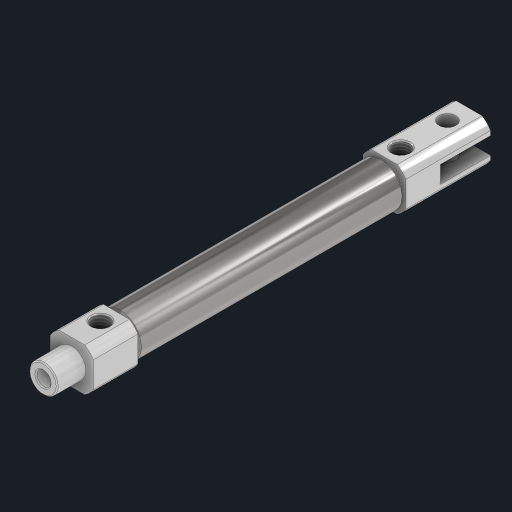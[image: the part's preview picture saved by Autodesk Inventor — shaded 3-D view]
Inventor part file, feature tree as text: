
AUTODESK INVENTOR PART (.ipt)
format: ipt  version: 2023 (Build 270158030, 158C)  size: 207,872 bytes
history: mixed  units: in
note: dims shown in document units (in); Inventor stores cm internally (conversion verified against a paired STEP export)
features: thread x2, extrude x1, sketch x1, other x1, imported_body x1
ambient origin geometry x8: Origin, YZ Plane, XZ Plane, XY Plane, X Axis, Y Axis, Z Axis, Center Point
bodies: Solid1 (imported_parasolid)
feature tree (6):
  thread  "Thread1"  [1 undecoded]
  thread  "Thread2"  [1 undecoded]
  extrude  "Extrusion3"  [1 undecoded]
  sketch  "Sketch3"  dims[d8=0.0in d9=0.0in]
  other  "DetailChamfer"
  imported_body  NMx_Import_Brep_tag  [imported B-rep: ~35 faces, bbox_mm=[12.0, 12.0, 104.093597]]
note: 3 required parameter values undecoded (feature->parameter linkage not recoverable at this tier; creation-order binding heuristic only, values carry confidence <= 0.55)
